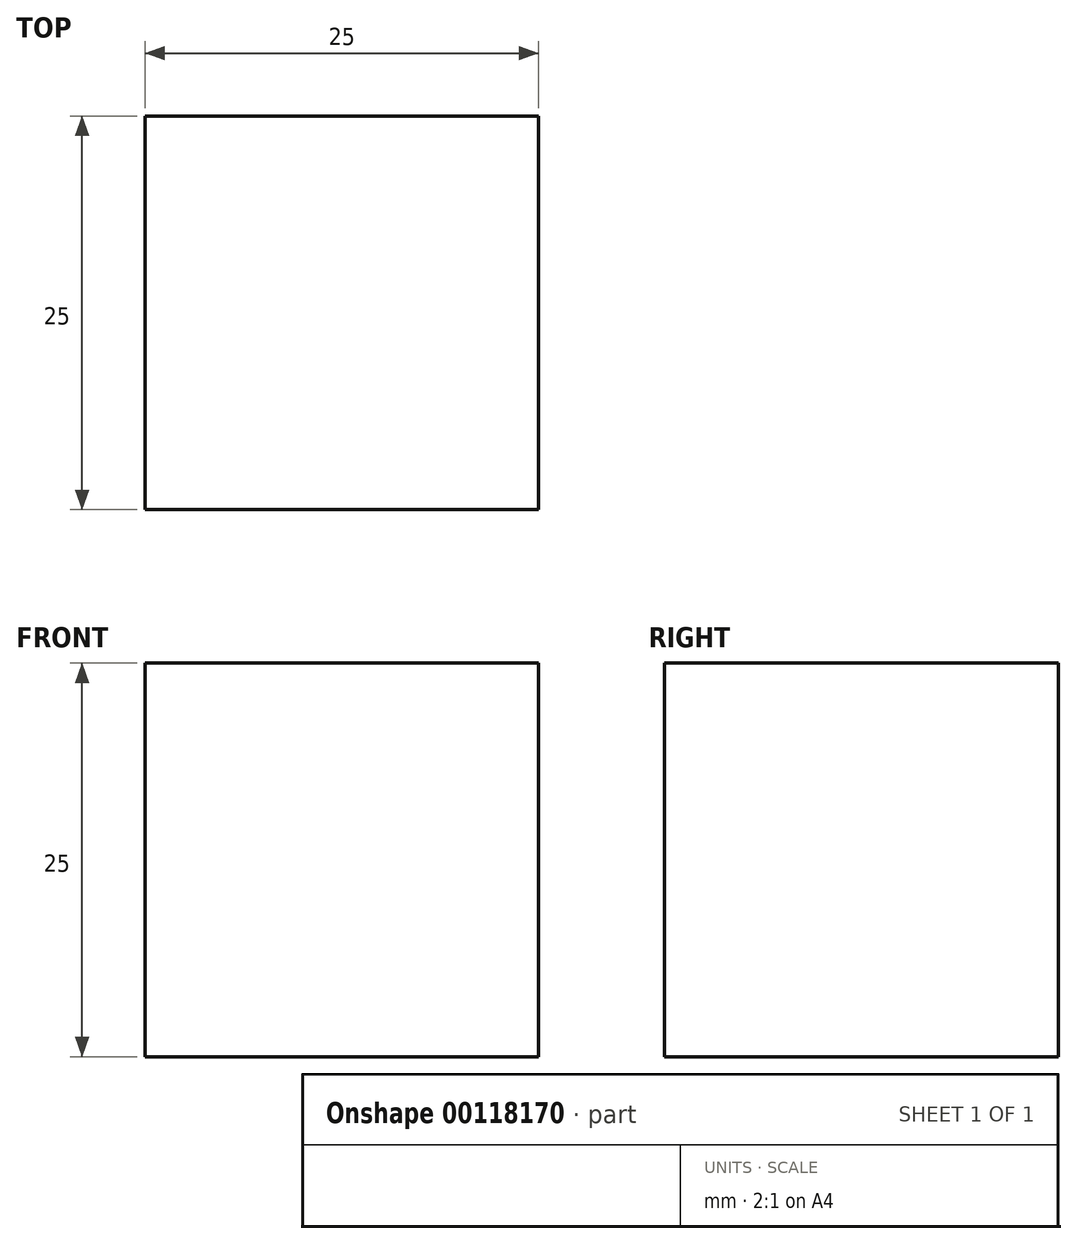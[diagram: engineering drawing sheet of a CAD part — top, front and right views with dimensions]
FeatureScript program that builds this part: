
annotation { "Feature Type Name" : "Feature", "Feature Type Description" : "" }
export const myFeature = defineFeature(function(context is Context, id is Id, definition is map)
    precondition{}
    {
        {
            var Q0;
            Q0=qCreatedBy(makeId("Top.planeOp"),FACE);
            var sketch = newSketch(context, id + "F0", { "sketchPlane" : qUnion([Q0])});
            skLineSegment(sketch, "E0.bottom", {"start": v(0, 0) * mm, "end": v(25, 0) * mm});
            skLineSegment(sketch, "E0.top", {"start": v(0, 25) * mm, "end": v(25, 25) * mm});
            skLineSegment(sketch, "E0.left", {"start": v(0, 0) * mm, "end": v(0, 25) * mm});
            skLineSegment(sketch, "E0.right", {"start": v(25, 0) * mm, "end": v(25, 25) * mm});
            skSolve(sketch);
        }
        {
            var Q0;
            Q0 = qSketchRegion(id + "F0", true);
            extrude(context, id + "F1", {"entities" : qUnion([Q0]), "depth" : 25 * mm});
        }
    });
